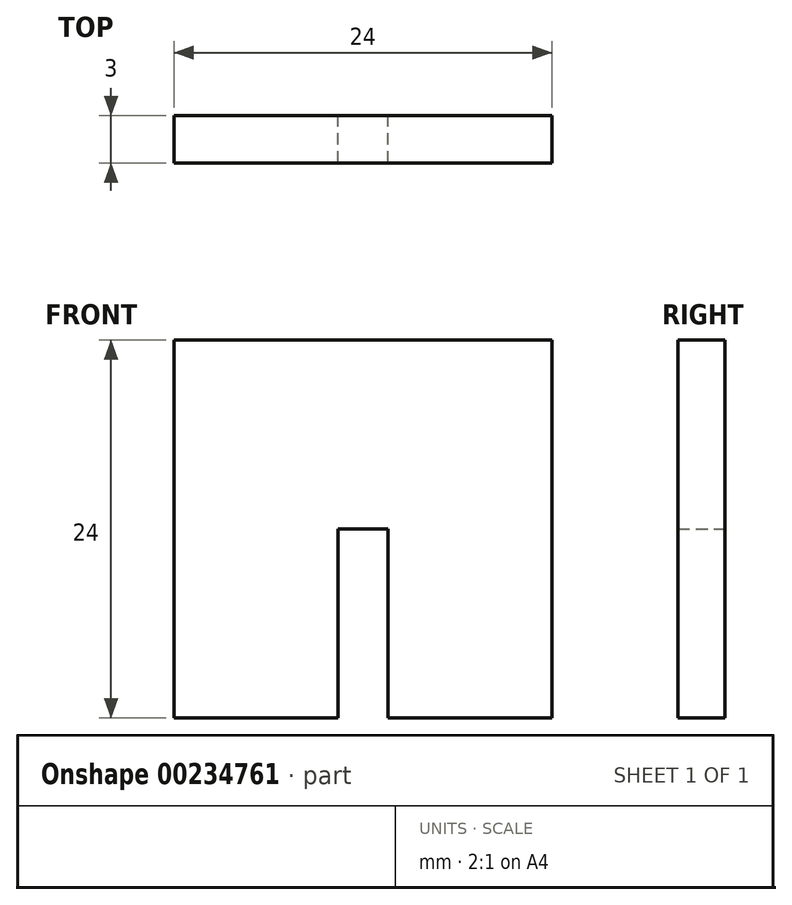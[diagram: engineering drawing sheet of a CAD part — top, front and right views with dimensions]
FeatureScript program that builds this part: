
annotation { "Feature Type Name" : "Feature", "Feature Type Description" : "" }
export const myFeature = defineFeature(function(context is Context, id is Id, definition is map)
    precondition{}
    {
        {
            var Q0;
            Q0=qCreatedBy(makeId("Front.planeOp"),FACE);
            var sketch = newSketch(context, id + "F0", { "sketchPlane" : qUnion([Q0])});
            skLineSegment(sketch, "E0.top", {"start": v(-10.83, 24.53) * mm, "end": v(13.17, 24.53) * mm});
            skLineSegment(sketch, "E0.left", {"start": v(-10.83, 0.53) * mm, "end": v(-10.83, 24.53) * mm});
            skLineSegment(sketch, "E0.right", {"start": v(13.17, 0.53) * mm, "end": v(13.17, 24.53) * mm});
            skLineSegment(sketch, "E1.top", {"start": v(-0.43, 12.53) * mm, "end": v(2.77, 12.53) * mm});
            skLineSegment(sketch, "E1.left", {"start": v(-0.43, 0.53) * mm, "end": v(-0.43, 12.53) * mm});
            skLineSegment(sketch, "E1.right", {"start": v(2.77, 0.53) * mm, "end": v(2.77, 12.53) * mm});
            skLineSegment(sketch, "E2", {"start": v(-10.83, 0.53) * mm, "end": v(-0.43, 0.53) * mm});
            skLineSegment(sketch, "E3", {"start": v(2.77, 0.53) * mm, "end": v(13.17, 0.53) * mm});
            skSolve(sketch);
        }
        {
            var Q0;
            Q0 = qSketchRegion(id + "F0", true);
            extrude(context, id + "F1", {"entities" : qUnion([Q0]), "depth" : 3 * mm});
        }
    });
